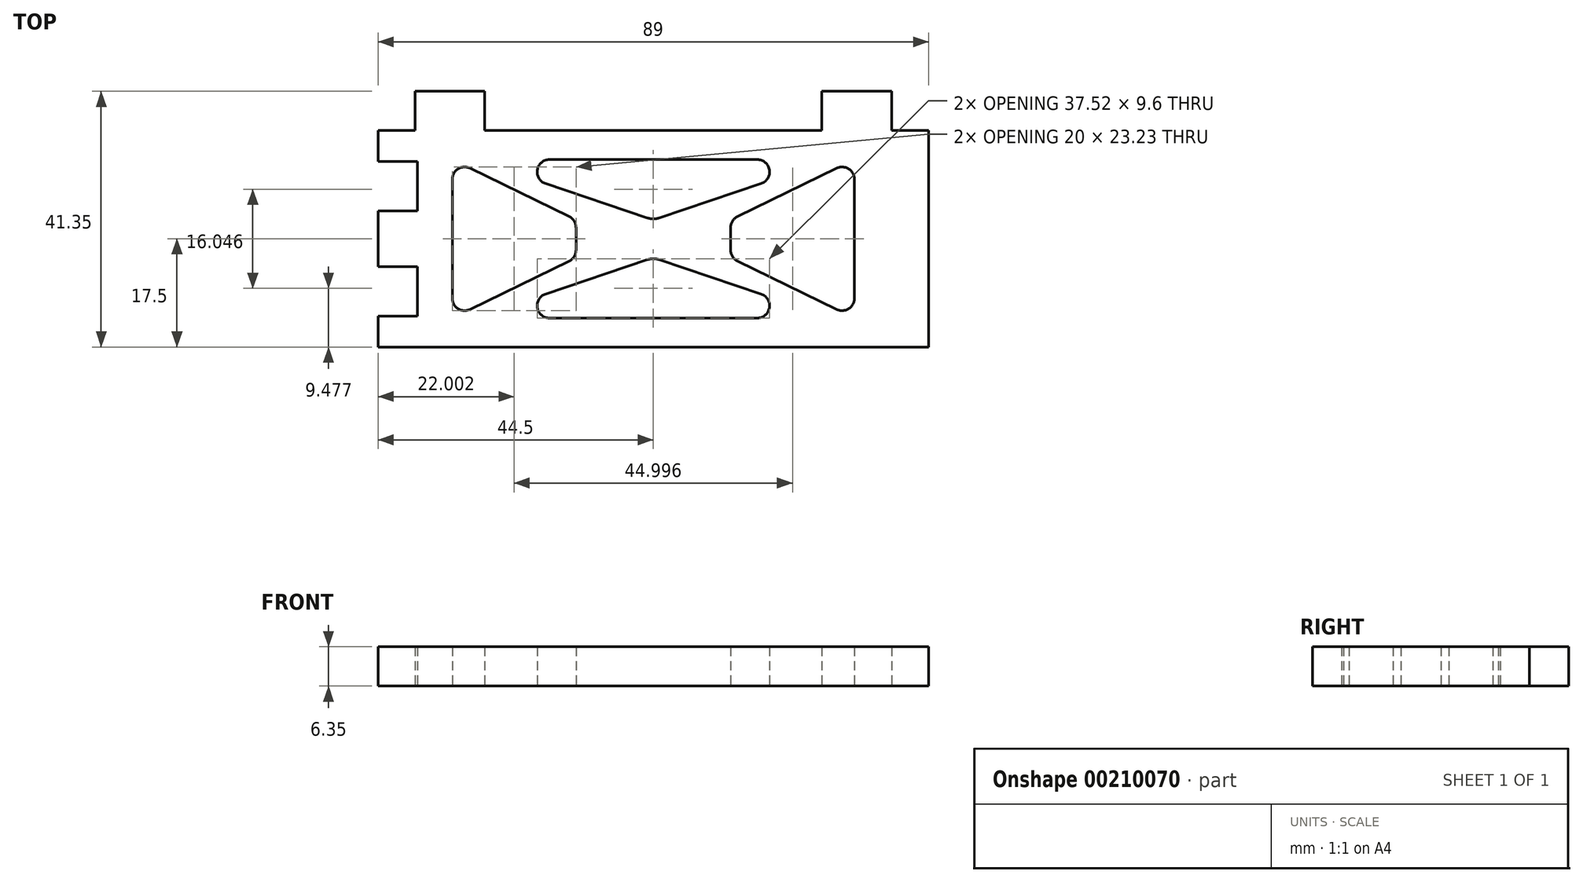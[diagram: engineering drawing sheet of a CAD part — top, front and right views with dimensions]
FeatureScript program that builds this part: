
annotation { "Feature Type Name" : "Feature", "Feature Type Description" : "" }
export const myFeature = defineFeature(function(context is Context, id is Id, definition is map)
    precondition{}
    {
        {
            var Q0;
            Q0=qCreatedBy(makeId("Top.planeOp"),FACE);
            var sketch = newSketch(context, id + "F0", { "sketchPlane" : qUnion([Q0])});
            skPoint(sketch, "E0.middle", {"position": v(0, 0) * mm});
            skLineSegment(sketch, "E1.bottom", {"start": v(-44.5, 17.5) * mm, "end": v(44.5, 17.5) * mm});
            skLineSegment(sketch, "E1.top", {"start": v(-44.5, -17.5) * mm, "end": v(44.5, -17.5) * mm});
            skLineSegment(sketch, "E1.left", {"start": v(-44.5, 17.5) * mm, "end": v(-44.5, -17.5) * mm});
            skLineSegment(sketch, "E1.right", {"start": v(44.5, 17.5) * mm, "end": v(44.5, -17.5) * mm});
            skLineSegment(sketch, "E2.bottom", {"start": v(-38.5, -17.5) * mm, "end": v(-27.25, -17.5) * mm});
            skLineSegment(sketch, "E2.top", {"start": v(-38.5, -23.85) * mm, "end": v(-27.25, -23.85) * mm});
            skLineSegment(sketch, "E2.left", {"start": v(-38.5, -17.5) * mm, "end": v(-38.5, -23.85) * mm});
            skLineSegment(sketch, "E2.right", {"start": v(-27.25, -17.5) * mm, "end": v(-27.25, -23.85) * mm});
            skLineSegment(sketch, "E3.bottom", {"start": v(38.5, -17.5) * mm, "end": v(27.25, -17.5) * mm});
            skLineSegment(sketch, "E3.top", {"start": v(38.5, -23.85) * mm, "end": v(27.25, -23.85) * mm});
            skLineSegment(sketch, "E3.left", {"start": v(38.5, -17.5) * mm, "end": v(38.5, -23.85) * mm});
            skLineSegment(sketch, "E3.right", {"start": v(27.25, -17.5) * mm, "end": v(27.25, -23.85) * mm});
            skLineSegment(sketch, "E4", {"start": v(-44.5, 0) * mm, "end": v(44.5, 0) * mm, "construction": true});
            skLineSegment(sketch, "E5", {"start": v(0, 17.5) * mm, "end": v(0, -17.5) * mm, "construction": true});
            skLineSegment(sketch, "E6", {"start": v(-32.5, 0) * mm, "end": v(-32.5, -9.62) * mm});
            skLineSegment(sketch, "E7", {"start": v(-29.62, -11.42) * mm, "end": v(-13.62, -3.6) * mm});
            skLineSegment(sketch, "E8", {"start": v(-12.5, -1.8) * mm, "end": v(-12.5, 0) * mm});
            skLineSegment(sketch, "E9", {"start": v(-17.42, -8.93) * mm, "end": v(-0.96, -3.38) * mm});
            skLineSegment(sketch, "E10", {"start": v(-16.78, -12.82) * mm, "end": v(0, -12.82) * mm});
            skArc(sketch, "E11.filletArc", {"start": v(-32.5, -9.62) * mm, "mid": v(-31.56, -11.32) * mm, "end": v(-29.62, -11.42) * mm});
            skArc(sketch, "E12.filletArc", {"start": v(-13.62, -3.6) * mm, "mid": v(-12.8, -2.87) * mm, "end": v(-12.5, -1.8) * mm});
            skPoint(sketch, "E13.visualSharp", {"position": v(-29, -12.82) * mm});
            skArc(sketch, "E13.filletArc", {"start": v(-17.42, -8.93) * mm, "mid": v(-18.76, -11.14) * mm, "end": v(-16.78, -12.82) * mm});
            skPoint(sketch, "E14.orphan", {"position": v(-12.5, -3.06) * mm});
            skPoint(sketch, "E15.orphan", {"position": v(-32.5, -12.82) * mm});
            skLineSegment(sketch, "E16.MirrorCS", {"start": v(16.78, -12.82) * mm, "end": v(0, -12.82) * mm});
            skArc(sketch, "E17.MirrorCS", {"start": v(17.42, -8.93) * mm, "mid": v(18.76, -11.14) * mm, "end": v(16.78, -12.82) * mm});
            skLineSegment(sketch, "E18.MirrorCS", {"start": v(17.42, -8.93) * mm, "end": v(0.96, -3.38) * mm});
            skLineSegment(sketch, "E19.MirrorCS", {"start": v(12.5, -1.8) * mm, "end": v(12.5, 0) * mm});
            skArc(sketch, "E20.MirrorCS", {"start": v(13.62, -3.6) * mm, "mid": v(12.8, -2.87) * mm, "end": v(12.5, -1.8) * mm});
            skLineSegment(sketch, "E21.MirrorCS", {"start": v(32.5, 0) * mm, "end": v(32.5, -9.62) * mm});
            skLineSegment(sketch, "E22.MirrorCS", {"start": v(29.62, -11.42) * mm, "end": v(13.62, -3.6) * mm});
            skArc(sketch, "E23.MirrorCS", {"start": v(32.5, -9.62) * mm, "mid": v(31.56, -11.32) * mm, "end": v(29.62, -11.42) * mm});
            skPoint(sketch, "E24.visualSharp", {"position": v(0, -3.06) * mm});
            skArc(sketch, "E24.filletArc", {"start": v(0.96, -3.38) * mm, "mid": v(0, -3.22) * mm, "end": v(-0.96, -3.38) * mm});
            skLineSegment(sketch, "E25.MirrorCS", {"start": v(-32.5, 0) * mm, "end": v(-32.5, 9.62) * mm});
            skArc(sketch, "E26.MirrorCS", {"start": v(-32.5, 9.62) * mm, "mid": v(-31.56, 11.32) * mm, "end": v(-29.62, 11.42) * mm});
            skLineSegment(sketch, "E27.MirrorCS", {"start": v(-29.62, 11.42) * mm, "end": v(-13.62, 3.6) * mm});
            skLineSegment(sketch, "E28.MirrorCS", {"start": v(-12.5, 1.8) * mm, "end": v(-12.5, 0) * mm});
            skArc(sketch, "E29.MirrorCS", {"start": v(-13.62, 3.6) * mm, "mid": v(-12.8, 2.87) * mm, "end": v(-12.5, 1.8) * mm});
            skArc(sketch, "E30.MirrorCS", {"start": v(0.96, 3.38) * mm, "mid": v(0, 3.22) * mm, "end": v(-0.96, 3.38) * mm});
            skLineSegment(sketch, "E31.MirrorCS", {"start": v(-17.42, 8.93) * mm, "end": v(-0.96, 3.38) * mm});
            skArc(sketch, "E32.MirrorCS", {"start": v(-17.42, 8.93) * mm, "mid": v(-18.76, 11.14) * mm, "end": v(-16.78, 12.82) * mm});
            skLineSegment(sketch, "E33.MirrorCS", {"start": v(-16.78, 12.82) * mm, "end": v(0, 12.82) * mm});
            skLineSegment(sketch, "E34.MirrorCS", {"start": v(16.78, 12.82) * mm, "end": v(0, 12.82) * mm});
            skArc(sketch, "E35.MirrorCS", {"start": v(17.42, 8.93) * mm, "mid": v(18.76, 11.14) * mm, "end": v(16.78, 12.82) * mm});
            skLineSegment(sketch, "E36.MirrorCS", {"start": v(17.42, 8.93) * mm, "end": v(0.96, 3.38) * mm});
            skLineSegment(sketch, "E37.MirrorCS", {"start": v(12.5, 1.8) * mm, "end": v(12.5, 0) * mm});
            skArc(sketch, "E38.MirrorCS", {"start": v(13.62, 3.6) * mm, "mid": v(12.8, 2.87) * mm, "end": v(12.5, 1.8) * mm});
            skLineSegment(sketch, "E39.MirrorCS", {"start": v(29.62, 11.42) * mm, "end": v(13.62, 3.6) * mm});
            skLineSegment(sketch, "E40.MirrorCS", {"start": v(32.5, 0) * mm, "end": v(32.5, 9.62) * mm});
            skArc(sketch, "E41.MirrorCS", {"start": v(32.5, 9.62) * mm, "mid": v(31.56, 11.32) * mm, "end": v(29.62, 11.42) * mm});
            skLineSegment(sketch, "E42.bottom", {"start": v(-44.5, 12.5) * mm, "end": v(-38.15, 12.5) * mm});
            skLineSegment(sketch, "E42.top", {"start": v(-44.5, 4.5) * mm, "end": v(-38.15, 4.5) * mm});
            skLineSegment(sketch, "E42.left", {"start": v(-44.5, 12.5) * mm, "end": v(-44.5, 4.5) * mm});
            skLineSegment(sketch, "E42.right", {"start": v(-38.15, 12.5) * mm, "end": v(-38.15, 4.5) * mm});
            skLineSegment(sketch, "E43.bottom", {"start": v(-44.5, -4.5) * mm, "end": v(-38.15, -4.5) * mm});
            skLineSegment(sketch, "E43.top", {"start": v(-44.5, -12.5) * mm, "end": v(-38.15, -12.5) * mm});
            skLineSegment(sketch, "E43.left", {"start": v(-44.5, -4.5) * mm, "end": v(-44.5, -12.5) * mm});
            skLineSegment(sketch, "E43.right", {"start": v(-38.15, -4.5) * mm, "end": v(-38.15, -12.5) * mm});
            skLineSegment(sketch, "E44.MirrorCS", {"start": v(38.5, 17.5) * mm, "end": v(38.5, 23.85) * mm});
            skLineSegment(sketch, "E45.MirrorCS", {"start": v(38.5, 23.85) * mm, "end": v(27.25, 23.85) * mm});
            skLineSegment(sketch, "E46.MirrorCS", {"start": v(27.25, 17.5) * mm, "end": v(27.25, 23.85) * mm});
            skLineSegment(sketch, "E47.MirrorCS", {"start": v(-27.25, 17.5) * mm, "end": v(-27.25, 23.85) * mm});
            skLineSegment(sketch, "E48.MirrorCS", {"start": v(-38.5, 17.5) * mm, "end": v(-38.5, 23.85) * mm});
            skLineSegment(sketch, "E49.MirrorCS", {"start": v(-38.5, 23.85) * mm, "end": v(-27.25, 23.85) * mm});
            skSolve(sketch);
        }
        {
            var Q0;
            Q0=makeQuery(id+"F0.imprint","IMPRINT",FACE,{"disambiguationData":[TD([[makeQuery(id+"F0.imprint","IMPRINT",EDGE,{"derivedFrom":sQuery(id+"F0.wireOp",EDGE,"E2.bottom")}),-1.0]])]});
            var Q1;
            Q1=makeQuery(id+"F0.imprint","IMPRINT",FACE,{"disambiguationData":[TD([[makeQuery(id+"F0.imprint","IMPRINT",EDGE,{"derivedFrom":sQuery(id+"F0.wireOp",EDGE,"E3.bottom")}),1.0]])]});
            var Q2;
            {var subQ10=sQuery(id+"F0.wireOp",EDGE,"E1.bottom");Q2=makeQuery(id+"F0.imprint","IMPRINT",FACE,{"disambiguationData":[TD([[makeQuery(id+"F0.imprint","IMPRINT",EDGE,{"derivedFrom":subQ10}),-1.0]])]});}
            var Q3;
            {var subQ0=sQuery(id+"F0.wireOp",EDGE,"E47.MirrorCS");Q3=makeQuery(id+"F0.imprint","IMPRINT",FACE,{"disambiguationData":[TD([[makeQuery(id+"F0.imprint","IMPRINT",EDGE,{"derivedFrom":subQ0}),1.0]])]});}
            var Q4;
            {var subQ0=sQuery(id+"F0.wireOp",EDGE,"E44.MirrorCS");Q4=makeQuery(id+"F0.imprint","IMPRINT",FACE,{"disambiguationData":[TD([[makeQuery(id+"F0.imprint","IMPRINT",EDGE,{"derivedFrom":subQ0}),1.0]])]});}
            extrude(context, id + "F1", {"entities" : qUnion([Q0, Q1, Q2, Q3, Q4]), "depth" : 6.35 * mm});
        }
    });
